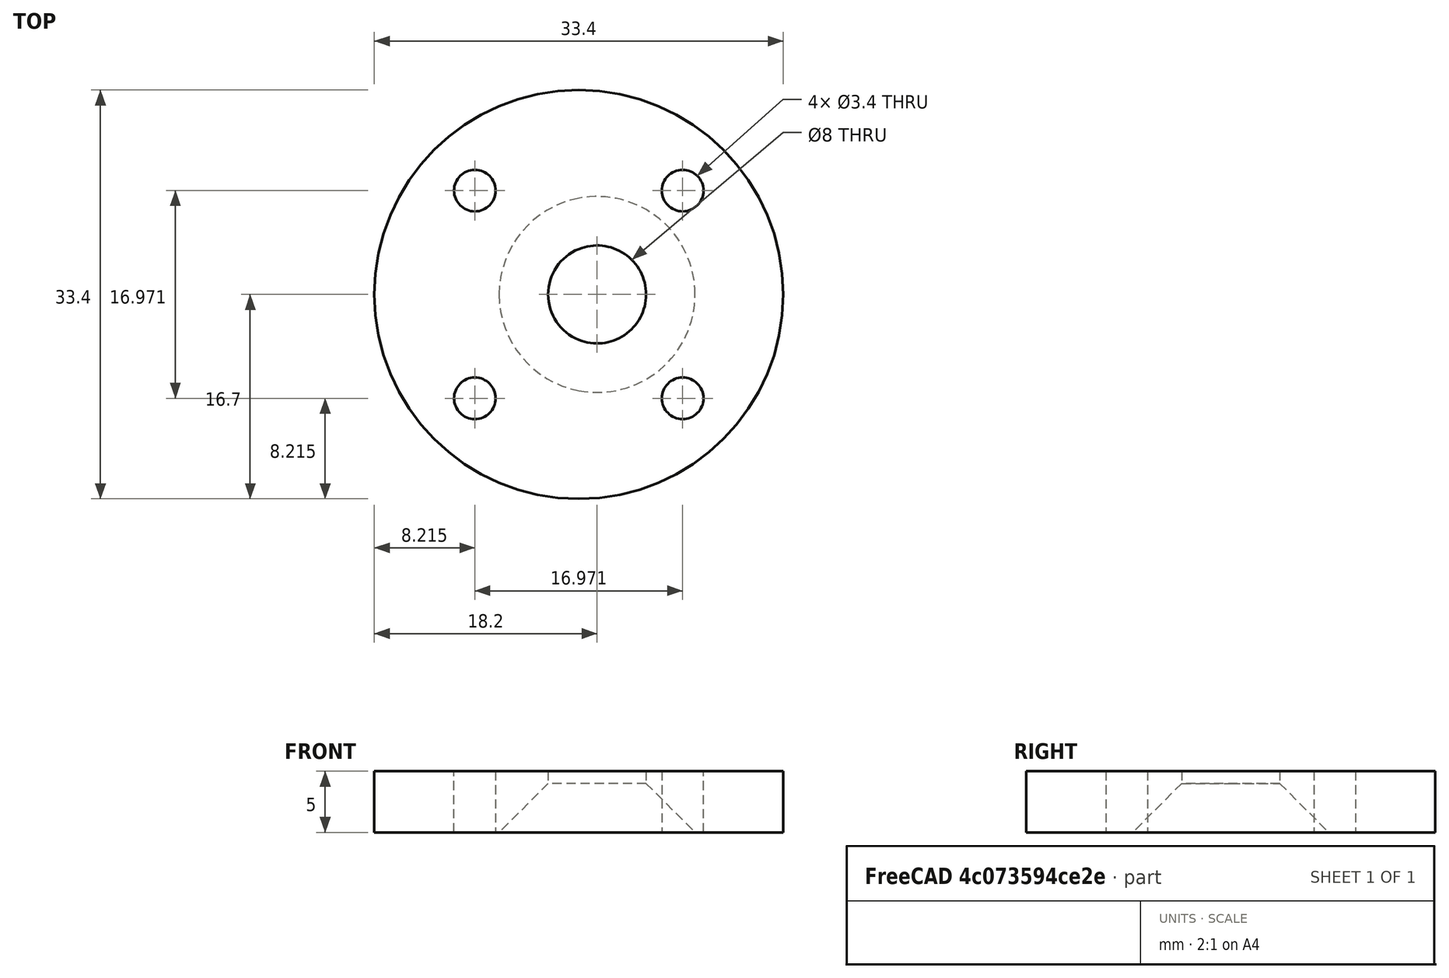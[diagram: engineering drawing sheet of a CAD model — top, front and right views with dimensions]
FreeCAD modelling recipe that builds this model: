
FCSTD DOCUMENT  (FreeCAD 0.19R24291 (Git))
Label: eccentric v3
License: All rights reserved
LicenseURL: http://en.wikipedia.org/wiki/All_rights_reserved
objects: Sketcher::SketchObject×2, PartDesign::Mirrored×2, PartDesign::Pad×1, PartDesign::MultiTransform×1, PartDesign::Groove×1, PartDesign::Body×1, Mesh::Feature×1
note: 10 computed .brp shape members not serialized (recipe doc carries the construction recipe); baked Part::Feature solids carry a one-line shape summary decoded from their .brp

FEATURE [Sketcher::SketchObject] Sketch
  FullyConstrained = true
  MapMode = 5
  Support = -> [XY_Plane]
  sketch-geometry (6):
    g0: ArcOfCircle CenterX=0 CenterY=0 CenterZ=0 NormalX=0 NormalY=0 NormalZ=1 AngleXU=0 Radius=16.7 StartAngle=0 EndAngle=1.5708
    g1: Circle CenterX=8.48528 CenterY=8.48528 CenterZ=0 NormalX=0 NormalY=0 NormalZ=1 AngleXU=0 Radius=1.7
    g2: LineSegment StartX=8.48528 StartY=8.48528 StartZ=0 EndX=0 EndY=8.48528 EndZ=0
    g3: LineSegment StartX=8.48528 StartY=8.48528 StartZ=0 EndX=8.48528 EndY=0 EndZ=0
    g4: LineSegment StartX=1e-15 StartY=16.7 StartZ=0 EndX=0 EndY=0 EndZ=0
    g5: LineSegment StartX=0 StartY=0 StartZ=0 EndX=16.7 EndY=0 EndZ=0
  constraints (17):
    c: Coincident(g0,g-1)
    c: PointOnObject(g0,g-1)
    c: PointOnObject(g0,g-2)
    c: Coincident(g2,g1)
    c: PointOnObject(g2,g-2)
    c: Horizontal(g2)
    c: Coincident(g3,g1)
    c: PointOnObject(g3,g-1)
    c: Vertical(g3)
    c: Equal(g3,g2)
    c: Distance(g1,g0) = 12
    c: Diameter(g1) = 3.4
    c: Coincident(g4,g0)
    c: Coincident(g4,g0)
    c: Coincident(g5,g0)
    c: Coincident(g5,g0)
    c: Diameter(g0) = 33.4
FEATURE [PartDesign::Pad] Pad
  Direction = (1,1,1)
  Length = 5
  Length2 = 100
  Profile = -> Sketch
  Type = 0
FEATURE [PartDesign::Mirrored] Mirrored
  MirrorPlane = -> Sketch [V_Axis]
FEATURE [PartDesign::Mirrored] Mirrored001
  MirrorPlane = -> Sketch [H_Axis]
FEATURE [PartDesign::MultiTransform] MultiTransform
  BaseFeature = -> Pad
  Originals = -> [Pad]
  Transformations = -> [Mirrored,Mirrored001]
FEATURE [Sketcher::SketchObject] Sketch001
  AttachmentOffset = pos=(1.5,0,0) rot=(0,0,1;0rad)
  FullyConstrained = true
  MapMode = 5
  Placement = pos=(1.5,0,0) rot=(1,0,0;1.5708rad)
  Support = -> [XZ_Plane]
  sketch-geometry (5):
    g0: LineSegment StartX=0 StartY=5 StartZ=0 EndX=4 EndY=5 EndZ=0
    g1: LineSegment StartX=4 StartY=5 StartZ=0 EndX=4 EndY=4 EndZ=0
    g2: LineSegment StartX=4 StartY=4 StartZ=0 EndX=8 EndY=0 EndZ=0
    g3: LineSegment StartX=8 StartY=0 StartZ=0 EndX=0 EndY=0 EndZ=0
    g4: LineSegment StartX=0 StartY=0 StartZ=0 EndX=0 EndY=5 EndZ=0
  constraints (14):
    c: PointOnObject(g0,g-2)
    c: Horizontal(g0)
    c: Coincident(g1,g0)
    c: Vertical(g1)
    c: Coincident(g2,g1)
    c: PointOnObject(g2,g-1)
    c: Coincident(g3,g2)
    c: Coincident(g3,g-1)
    c: Coincident(g4,g3)
    c: Coincident(g4,g0)
    c: Angle(g-2,g2) = 0.785398
    c: Distance(g1) = 1
    c: Distance(g0) = 4
    c: Distance(g4) = 5
FEATURE [PartDesign::Groove] Groove
  Angle = 360
  Axis = (0,-2e-16,1)
  Base = (1.5,0,0)
  BaseFeature = -> MultiTransform
  Profile = -> Sketch001
  ReferenceAxis = -> Sketch001 [V_Axis]
FEATURE [PartDesign::Body] Body
  Group = -> [Sketch,Pad,MultiTransform,Mirrored,Mirrored001,Sketch001,Groove]
  Origin = -> Origin
  Tip = -> Groove
FEATURE [Mesh::Feature] eccentric_v2_Body  label="eccentric v2-Body"
